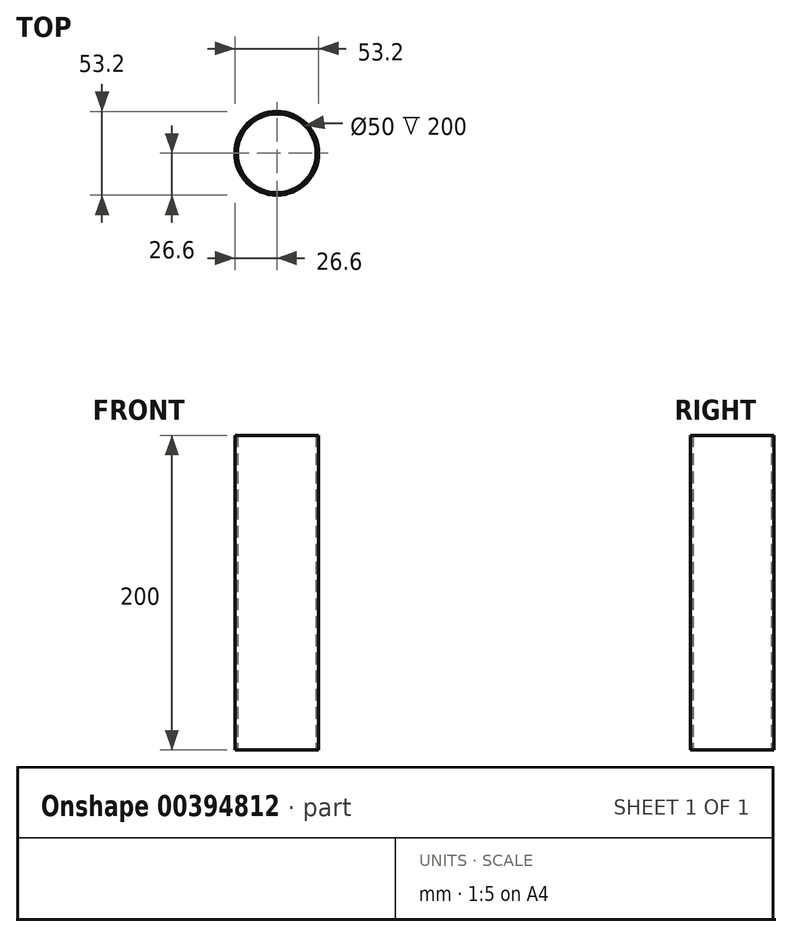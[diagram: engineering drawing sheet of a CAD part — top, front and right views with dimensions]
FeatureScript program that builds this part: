
annotation { "Feature Type Name" : "Feature", "Feature Type Description" : "" }
export const myFeature = defineFeature(function(context is Context, id is Id, definition is map)
    precondition{}
    {
        {
            var Q0;
            Q0=qCreatedBy(makeId("Top.planeOp"),FACE);
            var sketch = newSketch(context, id + "F0", { "sketchPlane" : qUnion([Q0])});
            skCircle(sketch, "E0", {"center": v(0, 0) * mm, "radius": 26.6 * mm});
            skCircle(sketch, "E1", {"center": v(0, 0) * mm, "radius": 25 * mm});
            skSolve(sketch);
        }
        {
            var Q0;
            Q0=makeQuery(id+"F0.imprint","IMPRINT",FACE,{"disambiguationData":[TD([[makeQuery(id+"F0.imprint","IMPRINT",EDGE,{"derivedFrom":sQuery(id+"F0.wireOp",EDGE,"E0")}),1.0]])]});
            extrude(context, id + "F1", {"entities" : qUnion([Q0]), "depth" : 200 * mm});
        }
    });
